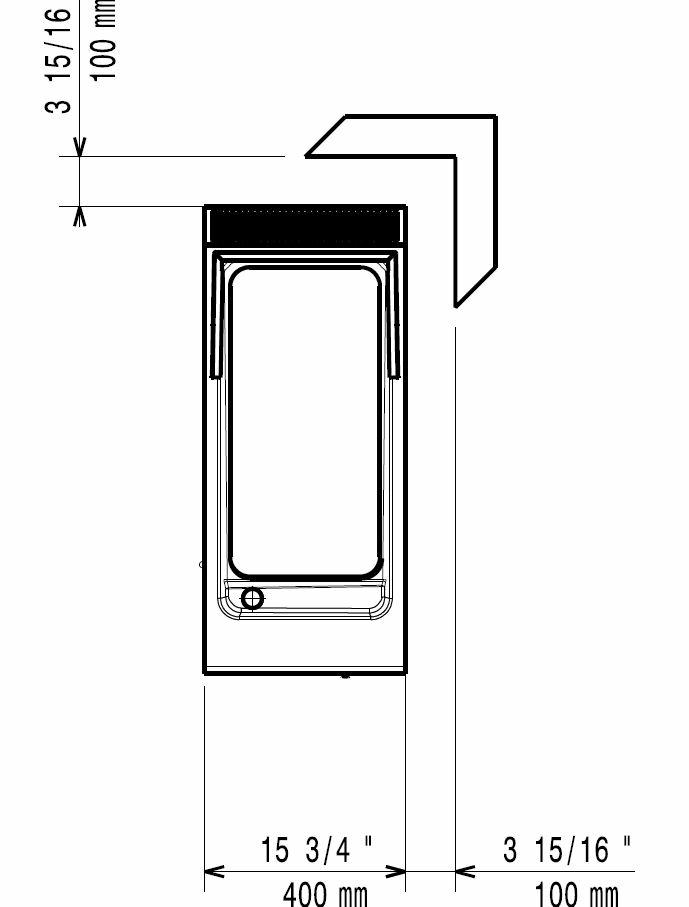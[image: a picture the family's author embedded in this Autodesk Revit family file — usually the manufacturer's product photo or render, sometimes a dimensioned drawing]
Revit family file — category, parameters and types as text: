
# Revit family: QF_ELECTROLUXPROFESSIONAL_391354_E9IILAAOMCA
name_source: partatom
category: Specialty Equipment
revit_build: Autodesk Revit 2018 (Build: 20190510_1515(x64)
units: mm (PartAtom-declared; Revit-internal decimal feet)

## family parameters
Always vertical = Yes
Cut with Voids When Loaded = No
Part Type = Normal
Room Calculation Point = No
Round Connector Dimension = Use Diameter
Shared = No
Work Plane-Based = No

## types (1)
- QF_ELECTROLUXPROFESSIONAL_391354_E9IILAAOMCA
    Depth = 930 mm  [stored 3.05118 ft]
    Description = 900XP HALF MODULE GAS FRY TOP, RIBBED SLOPED PLATE, MILD STEEL
    Direct Waste Size = 0"
    Gas Connection Height = 0 mm  [stored 0 ft]
    Gas Size = 1"
    HP = 0 HP
    Height = 410 mm
    Manufacturer = ELECTROLUX
    Model = 391049
    URL = www.electrolux.com/foodservice
    URL Cutsheet = www.electrolux.com/foodservice
    Watts = 0 W
    Weight in Pounds = 55
    Width = 400 mm  [stored 1.31234 ft]

note: [stored X ft] marks values corroborated as IEEE doubles in the binary element streams (Revit-internal decimal feet)

## geometry (parser evidence)
native form markers: Blend x28, Sweep x2
no freeform markers — native parametric forms only
